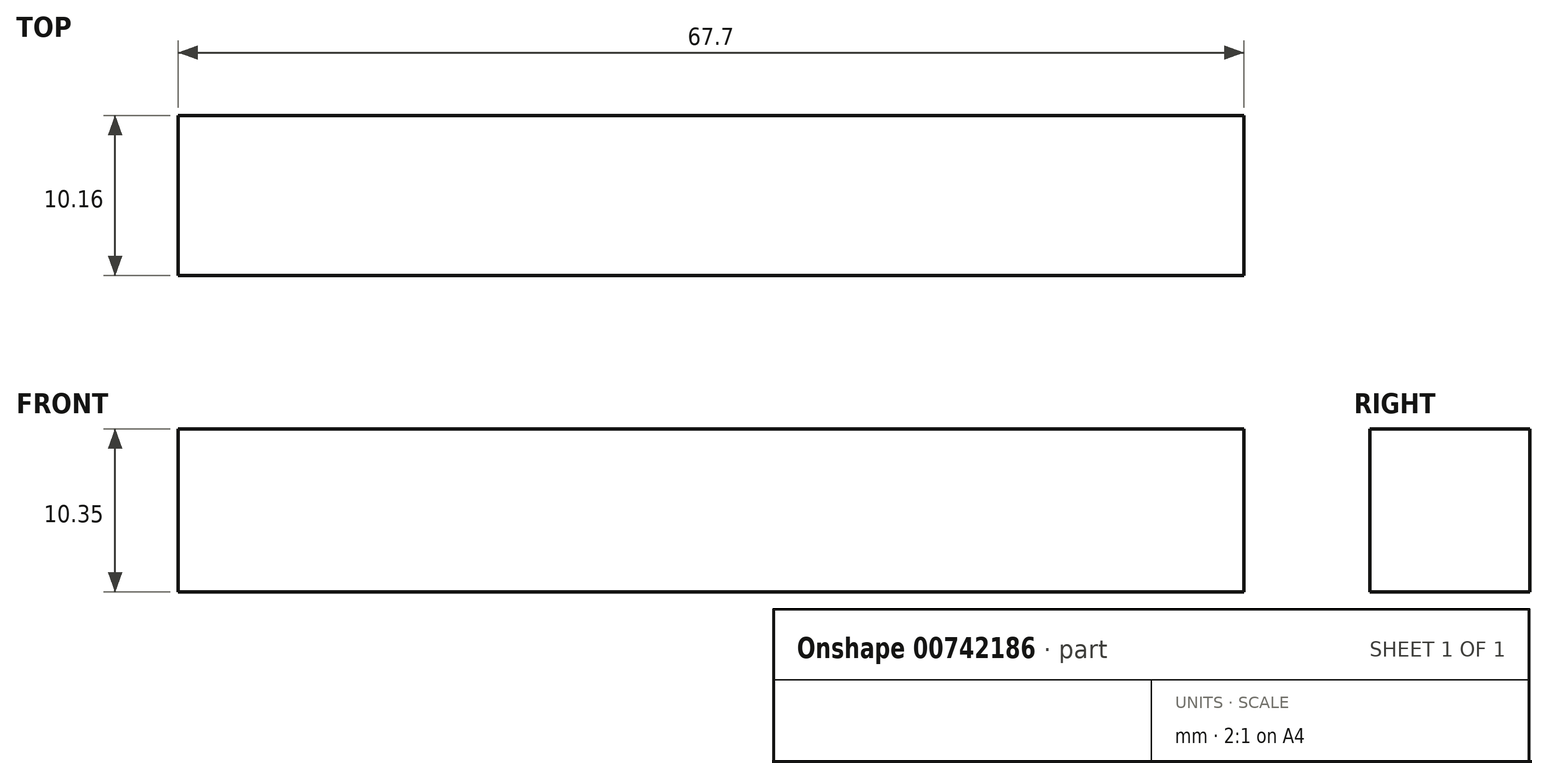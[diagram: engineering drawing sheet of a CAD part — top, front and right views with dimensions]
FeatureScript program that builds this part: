
annotation { "Feature Type Name" : "Feature", "Feature Type Description" : "" }
export const myFeature = defineFeature(function(context is Context, id is Id, definition is map)
    precondition{}
    {
        {
            var Q0;
            Q0=qCreatedBy(makeId("Front.planeOp"),FACE);
            var sketch = newSketch(context, id + "F0", { "sketchPlane" : qUnion([Q0])});
            skLineSegment(sketch, "E0.bottom", {"start": v(-20.84, -4.34) * mm, "end": v(46.86, -4.34) * mm});
            skLineSegment(sketch, "E0.top", {"start": v(-20.84, 6.01) * mm, "end": v(46.86, 6.01) * mm});
            skLineSegment(sketch, "E0.left", {"start": v(-20.84, -4.34) * mm, "end": v(-20.84, 6.01) * mm});
            skLineSegment(sketch, "E0.right", {"start": v(46.86, -4.34) * mm, "end": v(46.86, 6.01) * mm});
            skSolve(sketch);
        }
        {
            var Q0;
            Q0=makeQuery(id+"F0.imprint","IMPRINT",FACE,{"disambiguationData":[TD([[makeQuery(id+"F0.imprint","IMPRINT",EDGE,{"derivedFrom":sQuery(id+"F0.wireOp",EDGE,"E0.bottom")}),1.0]])]});
            extrude(context, id + "F1", {"entities" : qUnion([Q0]), "depth" : 10.16 * mm, "offsetDistance" : 25.4 * mm});
        }
    });
